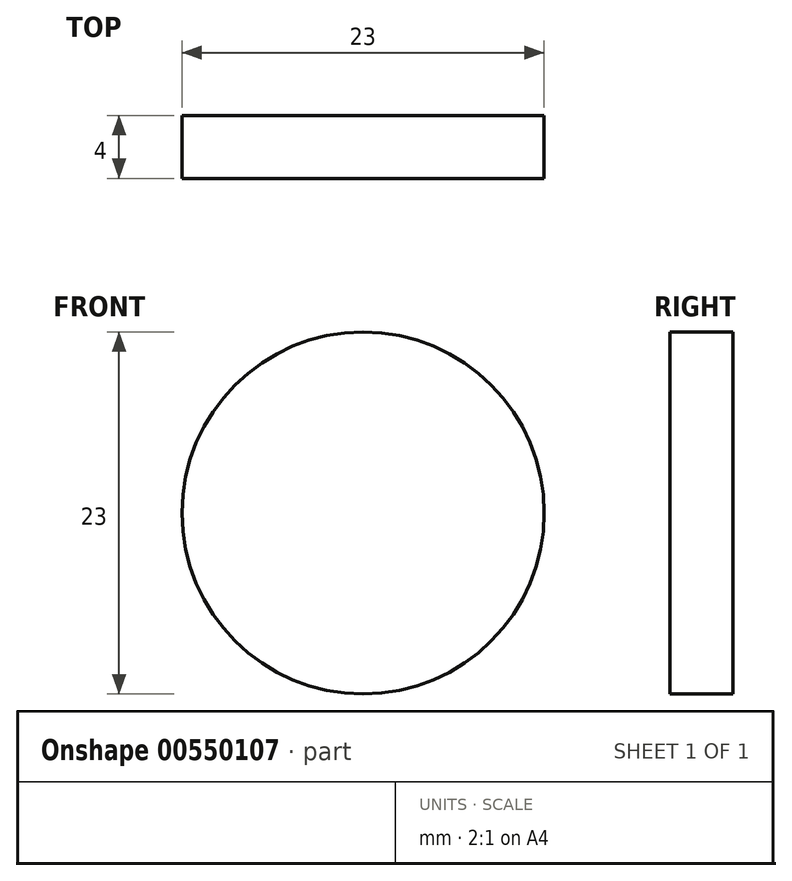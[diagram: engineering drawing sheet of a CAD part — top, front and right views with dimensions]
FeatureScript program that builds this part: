
annotation { "Feature Type Name" : "Feature", "Feature Type Description" : "" }
export const myFeature = defineFeature(function(context is Context, id is Id, definition is map)
    precondition{}
    {
        {
            var Q0;
            Q0=qCreatedBy(makeId("Front.planeOp"),FACE);
            var sketch = newSketch(context, id + "F0", { "sketchPlane" : qUnion([Q0])});
            skCircle(sketch, "E0", {"center": v(0, 0) * mm, "radius": 11.5 * mm});
            skSolve(sketch);
        }
        {
            var Q0;
            Q0=makeQuery(id+"F0.imprint","IMPRINT",FACE,{"disambiguationData":[TD([[makeQuery(id+"F0.imprint","IMPRINT",EDGE,{"derivedFrom":sQuery(id+"F0.wireOp",EDGE,"E0")}),1.0]])]});
            extrude(context, id + "F1", {"entities" : qUnion([Q0]), "depth" : 4 * mm, "offsetDistance" : 25 * mm});
        }
    });
